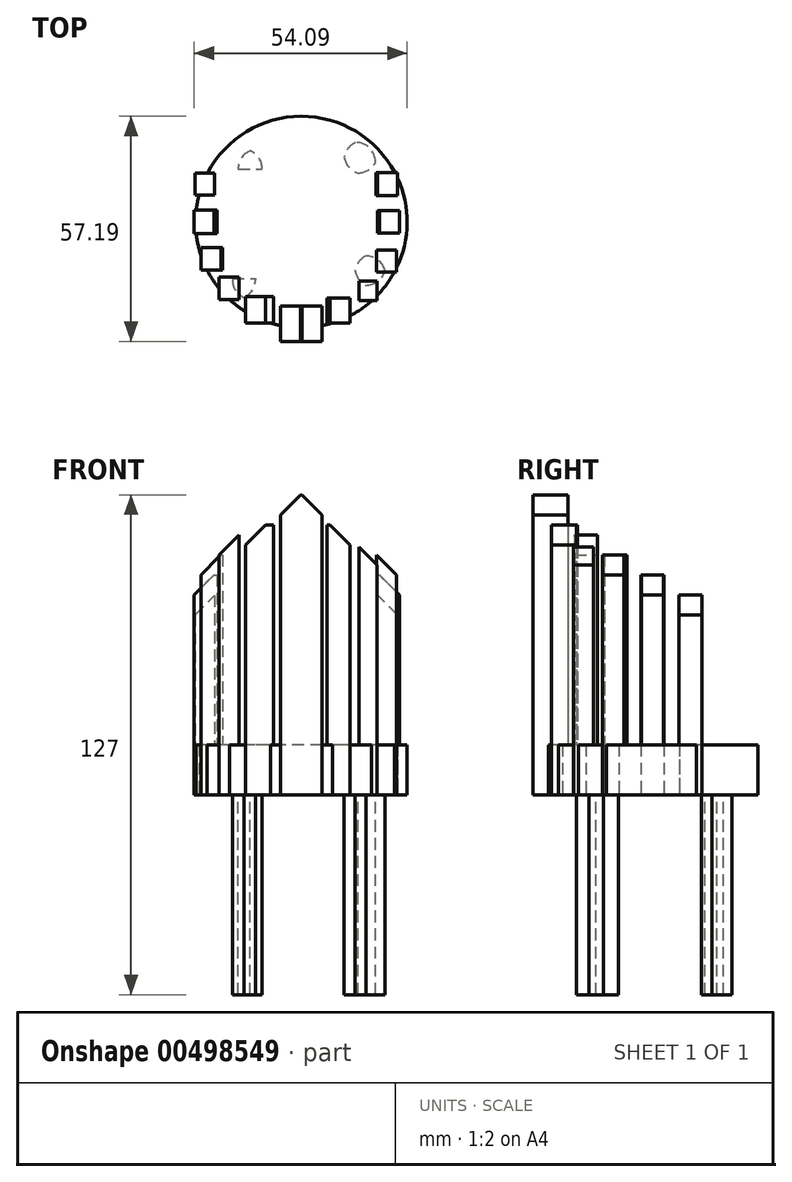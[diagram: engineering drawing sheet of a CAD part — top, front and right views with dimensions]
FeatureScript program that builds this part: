
annotation { "Feature Type Name" : "Feature", "Feature Type Description" : "" }
export const myFeature = defineFeature(function(context is Context, id is Id, definition is map)
    precondition{}
    {
        {
            var Q0;
            Q0=qCreatedBy(makeId("Top.planeOp"),FACE);
            var sketch = newSketch(context, id + "F0", { "sketchPlane" : qUnion([Q0])});
            skCircle(sketch, "E0", {"center": v(0, 0) * mm, "radius": 26.86 * mm});
            skSolve(sketch);
        }
        {
            var Q0;
            Q0=qSketchRegion(id+"F0",true);
            extrude(context, id + "F1", {"entities" : qUnion([Q0]), "depth" : 12.7 * mm});
        }
        {
            var Q0;
            Q0=qCreatedBy(makeId("Top.planeOp"),FACE);
            var sketch = newSketch(context, id + "F2", { "sketchPlane" : qUnion([Q0])});
            skLineSegment(sketch, "E1.bottom", {"start": v(21.46, -16.12) * mm, "end": v(13.6, -16.12) * mm});
            skLineSegment(sketch, "E1.top", {"start": v(21.46, -8.64) * mm, "end": v(13.6, -8.64) * mm});
            skLineSegment(sketch, "E1.left", {"start": v(21.46, -16.12) * mm, "end": v(21.46, -8.64) * mm});
            skLineSegment(sketch, "E1.right", {"start": v(13.6, -16.12) * mm, "end": v(13.6, -8.64) * mm});
            skPoint(sketch, "E1.middle", {"position": v(17.53, -12.38) * mm});
            skSolve(sketch);
        }
        {
            var Q0;
            Q0=qSketchRegion(id+"F2",true);
            extrude(context, id + "F3", {"entities" : qUnion([Q0]), "operationType" : NewBodyOperationType.ADD, "oppositeDirection" : true, "depth" : 50.8 * mm});
        }
        {
            var Q0;
            Q0=qCreatedBy(makeId("Top.planeOp"),FACE);
            var sketch = newSketch(context, id + "F4", { "sketchPlane" : qUnion([Q0])});
            skLineSegment(sketch, "E2.bottom", {"start": v(18.89, 12.44) * mm, "end": v(10.83, 12.44) * mm});
            skLineSegment(sketch, "E2.top", {"start": v(18.89, 20.22) * mm, "end": v(10.83, 20.22) * mm});
            skLineSegment(sketch, "E2.left", {"start": v(18.89, 12.44) * mm, "end": v(18.89, 20.22) * mm});
            skLineSegment(sketch, "E2.right", {"start": v(10.83, 12.44) * mm, "end": v(10.83, 20.22) * mm});
            skPoint(sketch, "E2.middle", {"position": v(14.86, 16.33) * mm});
            skSolve(sketch);
        }
        {
            var Q0;
            Q0=qSketchRegion(id+"F4",true);
            extrude(context, id + "F5", {"entities" : qUnion([Q0]), "operationType" : NewBodyOperationType.ADD, "oppositeDirection" : true, "depth" : 50.8 * mm});
        }
        {
            var Q0;
            Q0=makeQuery(id+"F5.opExtrude","SWEPT_EDGE",EDGE,{"disambiguationData":[OSD([sQuery(id+"F4.wireOp",EDGE,"E2.top"),sQuery(id+"F4.wireOp",EDGE,"E2.left")])]});
            fillet(context, id + "F6", {"entities" : qUnion([Q0]), "radius" : 5.08 * mm, "tangentPropagation" : true, "allowEdgeOverflow" : false});
        }
        {
            var Q0;
            Q0=makeQuery(id+"F5.opExtrude","SWEPT_EDGE",EDGE,{"disambiguationData":[OSD([sQuery(id+"F4.wireOp",EDGE,"E2.bottom"),sQuery(id+"F4.wireOp",EDGE,"E2.left")])]});
            fillet(context, id + "F7", {"entities" : qUnion([Q0]), "radius" : 5.08 * mm, "tangentPropagation" : true, "allowEdgeOverflow" : false});
        }
        {
            var Q0;
            Q0=makeQuery(id+"F3.opExtrude","SWEPT_EDGE",EDGE,{"disambiguationData":[OSD([sQuery(id+"F2.wireOp",EDGE,"E1.bottom"),sQuery(id+"F2.wireOp",EDGE,"E1.left")])]});
            var Q1;
            Q1=makeQuery(id+"F3.opExtrude","SWEPT_EDGE",EDGE,{"disambiguationData":[OSD([sQuery(id+"F2.wireOp",EDGE,"E1.top"),sQuery(id+"F2.wireOp",EDGE,"E1.left")])]});
            fillet(context, id + "F8", {"entities" : qUnion([Q0, Q1]), "radius" : 5.08 * mm, "tangentPropagation" : true, "allowEdgeOverflow" : false});
        }
        {
            var Q0;
            Q0=makeQuery(id+"F5.opExtrude","SWEPT_EDGE",EDGE,{"disambiguationData":[OSD([sQuery(id+"F4.wireOp",EDGE,"E2.top"),sQuery(id+"F4.wireOp",EDGE,"E2.right")])]});
            var Q1;
            Q1=makeQuery(id+"F5.opExtrude","SWEPT_EDGE",EDGE,{"disambiguationData":[OSD([sQuery(id+"F4.wireOp",EDGE,"E2.bottom"),sQuery(id+"F4.wireOp",EDGE,"E2.right")])]});
            var Q2;
            {var subQ0=sQuery(id+"F2.wireOp",EDGE,"E1.top");Q2=makeQuery(id+"F8.opFillet","BLEND_EDGE",EDGE,{"blendedFrom":[makeQuery(id+"F3.opExtrude","SWEPT_EDGE",EDGE,{"disambiguationData":[OSD([subQ0,sQuery(id+"F2.wireOp",EDGE,"E1.left")])]}),makeQuery(id+"F3.opExtrude","SWEPT_FACE",FACE,{"disambiguationData":[OSD([subQ0])]})],"blendedInto":[makeQuery(id+"F3.opExtrude","SWEPT_FACE",FACE,{"disambiguationData":[OSD([subQ0])]})]});}
            var Q3;
            Q3=makeQuery(id+"F3.opExtrude","SWEPT_EDGE",EDGE,{"disambiguationData":[OSD([sQuery(id+"F2.wireOp",EDGE,"E1.bottom"),sQuery(id+"F2.wireOp",EDGE,"E1.right")])]});
            fillet(context, id + "F9", {"entities" : qUnion([Q0, Q1, Q2, Q3]), "radius" : 5.08 * mm, "tangentPropagation" : true, "allowEdgeOverflow" : false});
        }
        {
            var Q0;
            Q0=makeQuery(id+"F3.opExtrude","SWEPT_EDGE",EDGE,{"disambiguationData":[OSD([sQuery(id+"F2.wireOp",EDGE,"E1.top"),sQuery(id+"F2.wireOp",EDGE,"E1.right")])]});
            fillet(context, id + "F10", {"entities" : qUnion([Q0]), "radius" : 5.08 * mm, "tangentPropagation" : true, "allowEdgeOverflow" : false});
        }
        {
            var Q0;
            Q0=qCreatedBy(makeId("Top.planeOp"),FACE);
            var sketch = newSketch(context, id + "F11", { "sketchPlane" : qUnion([Q0])});
            skLineSegment(sketch, "E3.bottom", {"start": v(-16.05, 18.5) * mm, "end": v(-9.93, 18.5) * mm});
            skLineSegment(sketch, "E3.top", {"start": v(-16.05, 13.36) * mm, "end": v(-9.93, 13.36) * mm});
            skLineSegment(sketch, "E3.left", {"start": v(-16.05, 18.5) * mm, "end": v(-16.05, 13.36) * mm});
            skLineSegment(sketch, "E3.right", {"start": v(-9.93, 18.5) * mm, "end": v(-9.93, 13.36) * mm});
            skPoint(sketch, "E3.middle", {"position": v(-12.99, 15.94) * mm});
            skSolve(sketch);
        }
        {
            var Q0;
            Q0=qSketchRegion(id+"F11",true);
            extrude(context, id + "F12", {"entities" : qUnion([Q0]), "operationType" : NewBodyOperationType.ADD, "oppositeDirection" : true, "depth" : 50.8 * mm});
        }
        {
            var Q0;
            Q0=qCreatedBy(makeId("Top.planeOp"),FACE);
            var sketch = newSketch(context, id + "F13", { "sketchPlane" : qUnion([Q0])});
            skLineSegment(sketch, "E4.bottom", {"start": v(-17.51, -14.37) * mm, "end": v(-11.66, -14.37) * mm});
            skLineSegment(sketch, "E4.top", {"start": v(-17.51, -19.72) * mm, "end": v(-11.66, -19.72) * mm});
            skLineSegment(sketch, "E4.left", {"start": v(-17.51, -14.37) * mm, "end": v(-17.51, -19.72) * mm});
            skLineSegment(sketch, "E4.right", {"start": v(-11.66, -14.37) * mm, "end": v(-11.66, -19.72) * mm});
            skPoint(sketch, "E4.middle", {"position": v(-14.59, -17.05) * mm});
            skSolve(sketch);
        }
        {
            var Q0;
            Q0=qSketchRegion(id+"F13",true);
            extrude(context, id + "F14", {"entities" : qUnion([Q0]), "operationType" : NewBodyOperationType.ADD, "oppositeDirection" : true, "depth" : 50.8 * mm});
        }
        {
            var Q0;
            Q0=makeQuery(id+"F14.opExtrude","SWEPT_EDGE",EDGE,{"disambiguationData":[OSD([sQuery(id+"F13.wireOp",EDGE,"E4.top"),sQuery(id+"F13.wireOp",EDGE,"E4.right")])]});
            var Q1;
            Q1=makeQuery(id+"F14.opExtrude","SWEPT_EDGE",EDGE,{"disambiguationData":[OSD([sQuery(id+"F13.wireOp",EDGE,"E4.top"),sQuery(id+"F13.wireOp",EDGE,"E4.left")])]});
            fillet(context, id + "F15", {"entities" : qUnion([Q0, Q1]), "radius" : 5.08 * mm, "tangentPropagation" : true, "allowEdgeOverflow" : false});
        }
        {
            var Q0;
            Q0=makeQuery(id+"F12.opExtrude","SWEPT_EDGE",EDGE,{"disambiguationData":[OSD([sQuery(id+"F11.wireOp",EDGE,"E3.bottom"),sQuery(id+"F11.wireOp",EDGE,"E3.right")])]});
            var Q1;
            Q1=makeQuery(id+"F12.opExtrude","SWEPT_EDGE",EDGE,{"disambiguationData":[OSD([sQuery(id+"F11.wireOp",EDGE,"E3.bottom"),sQuery(id+"F11.wireOp",EDGE,"E3.left")])]});
            fillet(context, id + "F16", {"entities" : qUnion([Q0, Q1]), "radius" : 5.08 * mm, "tangentPropagation" : true, "allowEdgeOverflow" : false});
        }
        {
            var Q0;
            Q0=qCreatedBy(makeId("Top.planeOp"),FACE);
            var sketch = newSketch(context, id + "F17", { "sketchPlane" : qUnion([Q0])});
            skLineSegment(sketch, "E5.bottom", {"start": v(-5.28, -30.33) * mm, "end": v(5.28, -30.33) * mm});
            skLineSegment(sketch, "E5.top", {"start": v(-5.28, -21.41) * mm, "end": v(5.28, -21.41) * mm});
            skLineSegment(sketch, "E5.left", {"start": v(-5.28, -30.33) * mm, "end": v(-5.28, -21.41) * mm});
            skLineSegment(sketch, "E5.right", {"start": v(5.28, -30.33) * mm, "end": v(5.28, -21.41) * mm});
            skPoint(sketch, "E5.middle", {"position": v(0, -25.87) * mm});
            skSolve(sketch);
        }
        {
            var Q0;
            Q0=qSketchRegion(id+"F17",true);
            extrude(context, id + "F18", {"entities" : qUnion([Q0]), "operationType" : NewBodyOperationType.ADD, "depth" : 76.2 * mm});
        }
        {
            var Q0;
            Q0=makeQuery(id+"F18.opExtrude","CAP_EDGE",EDGE,{"disambiguationData":[OSD([sQuery(id+"F17.wireOp",EDGE,"E5.left")])],"isStart":false});
            var Q1;
            Q1=makeQuery(id+"F18.opExtrude","CAP_EDGE",EDGE,{"disambiguationData":[OSD([sQuery(id+"F17.wireOp",EDGE,"E5.right")])],"isStart":false});
            chamfer(context, id + "F19", {"entities" : qUnion([Q0, Q1]), "width" : 5.08 * mm, "tangentPropagation" : true});
        }
        {
            var Q0;
            Q0=qCreatedBy(makeId("Top.planeOp"),FACE);
            var sketch = newSketch(context, id + "F20", { "sketchPlane" : qUnion([Q0])});
            skLineSegment(sketch, "E6.bottom", {"start": v(-14.13, -25.69) * mm, "end": v(-7.1, -25.69) * mm});
            skLineSegment(sketch, "E6.top", {"start": v(-14.13, -18.97) * mm, "end": v(-7.1, -18.97) * mm});
            skLineSegment(sketch, "E6.left", {"start": v(-14.13, -25.69) * mm, "end": v(-14.13, -18.97) * mm});
            skLineSegment(sketch, "E6.right", {"start": v(-7.1, -25.69) * mm, "end": v(-7.1, -18.97) * mm});
            skPoint(sketch, "E6.middle", {"position": v(-10.61, -22.33) * mm});
            skSolve(sketch);
        }
        {
            var Q0;
            Q0=qSketchRegion(id+"F20",true);
            extrude(context, id + "F21", {"entities" : qUnion([Q0]), "operationType" : NewBodyOperationType.ADD, "depth" : 68.58 * mm});
        }
        {
            var Q0;
            Q0=qCreatedBy(makeId("Top.planeOp"),FACE);
            var sketch = newSketch(context, id + "F22", { "sketchPlane" : qUnion([Q0])});
            skLineSegment(sketch, "E7.bottom", {"start": v(6.53, -25.66) * mm, "end": v(12.35, -25.66) * mm});
            skLineSegment(sketch, "E7.top", {"start": v(6.53, -19.34) * mm, "end": v(12.35, -19.34) * mm});
            skLineSegment(sketch, "E7.left", {"start": v(6.53, -25.66) * mm, "end": v(6.53, -19.34) * mm});
            skLineSegment(sketch, "E7.right", {"start": v(12.35, -25.66) * mm, "end": v(12.35, -19.34) * mm});
            skPoint(sketch, "E7.middle", {"position": v(9.44, -22.5) * mm});
            skSolve(sketch);
        }
        {
            var Q0;
            Q0=qSketchRegion(id+"F22",true);
            extrude(context, id + "F23", {"entities" : qUnion([Q0]), "operationType" : NewBodyOperationType.ADD, "depth" : 68.58 * mm});
        }
        {
            var Q0;
            Q0=makeQuery(id+"F23.opExtrude","CAP_EDGE",EDGE,{"disambiguationData":[OSD([sQuery(id+"F22.wireOp",EDGE,"E7.right")])],"isStart":false});
            var Q1;
            Q1=makeQuery(id+"F21.opExtrude","CAP_EDGE",EDGE,{"disambiguationData":[OSD([sQuery(id+"F20.wireOp",EDGE,"E6.left")])],"isStart":false});
            chamfer(context, id + "F24", {"entities" : qUnion([Q0, Q1]), "width" : 5.08 * mm, "tangentPropagation" : true});
        }
        {
            var Q0;
            Q0=qCreatedBy(makeId("Top.planeOp"),FACE);
            var sketch = newSketch(context, id + "F25", { "sketchPlane" : qUnion([Q0])});
            skLineSegment(sketch, "E8.bottom", {"start": v(-20.87, -19.75) * mm, "end": v(-15.87, -19.75) * mm});
            skLineSegment(sketch, "E8.top", {"start": v(-20.87, -14) * mm, "end": v(-15.87, -14) * mm});
            skLineSegment(sketch, "E8.left", {"start": v(-20.87, -19.75) * mm, "end": v(-20.87, -14) * mm});
            skLineSegment(sketch, "E8.right", {"start": v(-15.87, -19.75) * mm, "end": v(-15.87, -14) * mm});
            skPoint(sketch, "E8.middle", {"position": v(-18.37, -16.87) * mm});
            skSolve(sketch);
        }
        {
            var Q0;
            Q0=qSketchRegion(id+"F25",true);
            extrude(context, id + "F26", {"entities" : qUnion([Q0]), "operationType" : NewBodyOperationType.ADD, "depth" : 66.04 * mm});
        }
        {
            var Q0;
            Q0=makeQuery(id+"F26.opExtrude","CAP_EDGE",EDGE,{"disambiguationData":[OSD([sQuery(id+"F25.wireOp",EDGE,"E8.left")])],"isStart":false});
            chamfer(context, id + "F27", {"entities" : qUnion([Q0]), "width" : 5.08 * mm, "tangentPropagation" : true});
        }
        {
            var Q0;
            Q0=qCreatedBy(makeId("Top.planeOp"),FACE);
            var sketch = newSketch(context, id + "F28", { "sketchPlane" : qUnion([Q0])});
            skLineSegment(sketch, "E9.bottom", {"start": v(-25.47, -12.23) * mm, "end": v(-20, -12.23) * mm});
            skLineSegment(sketch, "E9.top", {"start": v(-25.47, -6.5) * mm, "end": v(-20, -6.5) * mm});
            skLineSegment(sketch, "E9.left", {"start": v(-25.47, -12.23) * mm, "end": v(-25.47, -6.5) * mm});
            skLineSegment(sketch, "E9.right", {"start": v(-20, -12.23) * mm, "end": v(-20, -6.5) * mm});
            skPoint(sketch, "E9.middle", {"position": v(-22.74, -9.37) * mm});
            skSolve(sketch);
        }
        {
            var Q0;
            Q0=qSketchRegion(id+"F28",true);
            extrude(context, id + "F29", {"entities" : qUnion([Q0]), "operationType" : NewBodyOperationType.ADD, "depth" : 60.96 * mm});
        }
        {
            var Q0;
            Q0=makeQuery(id+"F29.opExtrude","CAP_EDGE",EDGE,{"disambiguationData":[OSD([sQuery(id+"F28.wireOp",EDGE,"E9.left")])],"isStart":false});
            chamfer(context, id + "F30", {"entities" : qUnion([Q0]), "width" : 5.08 * mm, "tangentPropagation" : true});
        }
        {
            var Q0;
            Q0=qCreatedBy(makeId("Top.planeOp"),FACE);
            var sketch = newSketch(context, id + "F31", { "sketchPlane" : qUnion([Q0])});
            skLineSegment(sketch, "E10.bottom", {"start": v(-27.23, -2.95) * mm, "end": v(-21.46, -2.95) * mm});
            skLineSegment(sketch, "E10.top", {"start": v(-27.23, 2.95) * mm, "end": v(-21.46, 2.95) * mm});
            skLineSegment(sketch, "E10.left", {"start": v(-27.23, -2.95) * mm, "end": v(-27.23, 2.95) * mm});
            skLineSegment(sketch, "E10.right", {"start": v(-21.46, -2.95) * mm, "end": v(-21.46, 2.95) * mm});
            skPoint(sketch, "E10.middle", {"position": v(-24.35, 0) * mm});
            skSolve(sketch);
        }
        {
            var Q0;
            Q0=qCreatedBy(makeId("Top.planeOp"),FACE);
            var sketch = newSketch(context, id + "F32", { "sketchPlane" : qUnion([Q0])});
            skLineSegment(sketch, "E11.bottom", {"start": v(-26.94, 6.87) * mm, "end": v(-22, 6.87) * mm});
            skLineSegment(sketch, "E11.top", {"start": v(-26.94, 12.45) * mm, "end": v(-22, 12.45) * mm});
            skLineSegment(sketch, "E11.left", {"start": v(-26.94, 6.87) * mm, "end": v(-26.94, 12.45) * mm});
            skLineSegment(sketch, "E11.right", {"start": v(-22, 6.87) * mm, "end": v(-22, 12.45) * mm});
            skPoint(sketch, "E11.middle", {"position": v(-24.47, 9.66) * mm});
            skSolve(sketch);
        }
        {
            var Q0;
            Q0=qSketchRegion(id+"F31",true);
            extrude(context, id + "F33", {"entities" : qUnion([Q0]), "operationType" : NewBodyOperationType.ADD, "depth" : 55.88 * mm});
        }
        {
            var Q0;
            Q0=qSketchRegion(id+"F32",true);
            extrude(context, id + "F34", {"entities" : qUnion([Q0]), "operationType" : NewBodyOperationType.ADD, "depth" : 50.8 * mm});
        }
        {
            var Q0;
            Q0=makeQuery(id+"F33.opExtrude","CAP_EDGE",EDGE,{"disambiguationData":[OSD([sQuery(id+"F31.wireOp",EDGE,"E10.left")])],"isStart":false});
            chamfer(context, id + "F35", {"entities" : qUnion([Q0]), "width" : 5.08 * mm, "tangentPropagation" : true});
        }
        {
            var Q0;
            Q0=makeQuery(id+"F34.opExtrude","CAP_EDGE",EDGE,{"disambiguationData":[OSD([sQuery(id+"F32.wireOp",EDGE,"E11.left")])],"isStart":false});
            chamfer(context, id + "F36", {"entities" : qUnion([Q0]), "width" : 5.08 * mm, "tangentPropagation" : true});
        }
        {
            var Q0;
            Q0=qCreatedBy(makeId("Top.planeOp"),FACE);
            var sketch = newSketch(context, id + "F37", { "sketchPlane" : qUnion([Q0])});
            skLineSegment(sketch, "E12.bottom", {"start": v(14.7, -20.04) * mm, "end": v(19.27, -20.04) * mm});
            skLineSegment(sketch, "E12.top", {"start": v(14.7, -14.97) * mm, "end": v(19.27, -14.97) * mm});
            skLineSegment(sketch, "E12.left", {"start": v(14.7, -20.04) * mm, "end": v(14.7, -14.97) * mm});
            skLineSegment(sketch, "E12.right", {"start": v(19.27, -20.04) * mm, "end": v(19.27, -14.97) * mm});
            skPoint(sketch, "E12.middle", {"position": v(16.99, -17.5) * mm});
            skSolve(sketch);
        }
        {
            var Q0;
            Q0=qCreatedBy(makeId("Top.planeOp"),FACE);
            var sketch = newSketch(context, id + "F38", { "sketchPlane" : qUnion([Q0])});
            skLineSegment(sketch, "E13.bottom", {"start": v(19.16, -12.73) * mm, "end": v(24.2, -12.73) * mm});
            skLineSegment(sketch, "E13.top", {"start": v(19.16, -7.16) * mm, "end": v(24.2, -7.16) * mm});
            skLineSegment(sketch, "E13.left", {"start": v(19.16, -12.73) * mm, "end": v(19.16, -7.16) * mm});
            skLineSegment(sketch, "E13.right", {"start": v(24.2, -12.73) * mm, "end": v(24.2, -7.16) * mm});
            skPoint(sketch, "E13.middle", {"position": v(21.68, -9.94) * mm});
            skSolve(sketch);
        }
        {
            var Q0;
            Q0=qCreatedBy(makeId("Top.planeOp"),FACE);
            var sketch = newSketch(context, id + "F39", { "sketchPlane" : qUnion([Q0])});
            skLineSegment(sketch, "E14.bottom", {"start": v(19.3, -2.83) * mm, "end": v(24.9, -2.83) * mm});
            skLineSegment(sketch, "E14.top", {"start": v(19.3, 2.83) * mm, "end": v(24.9, 2.83) * mm});
            skLineSegment(sketch, "E14.left", {"start": v(19.3, -2.83) * mm, "end": v(19.3, 2.83) * mm});
            skLineSegment(sketch, "E14.right", {"start": v(24.9, -2.83) * mm, "end": v(24.9, 2.83) * mm});
            skPoint(sketch, "E14.middle", {"position": v(22.1, 0) * mm});
            skSolve(sketch);
        }
        {
            var Q0;
            Q0=qCreatedBy(makeId("Top.planeOp"),FACE);
            var sketch = newSketch(context, id + "F40", { "sketchPlane" : qUnion([Q0])});
            skLineSegment(sketch, "E15.bottom", {"start": v(18.93, 6.74) * mm, "end": v(24.44, 6.74) * mm});
            skLineSegment(sketch, "E15.top", {"start": v(18.93, 12.55) * mm, "end": v(24.44, 12.55) * mm});
            skLineSegment(sketch, "E15.left", {"start": v(18.93, 6.74) * mm, "end": v(18.93, 12.55) * mm});
            skLineSegment(sketch, "E15.right", {"start": v(24.44, 6.74) * mm, "end": v(24.44, 12.55) * mm});
            skPoint(sketch, "E15.middle", {"position": v(21.69, 9.64) * mm});
            skSolve(sketch);
        }
        {
            var Q0;
            Q0=qSketchRegion(id+"F37",true);
            extrude(context, id + "F41", {"entities" : qUnion([Q0]), "operationType" : NewBodyOperationType.ADD, "depth" : 63.5 * mm});
        }
        {
            var Q0;
            Q0=qSketchRegion(id+"F38",true);
            extrude(context, id + "F42", {"entities" : qUnion([Q0]), "operationType" : NewBodyOperationType.ADD, "depth" : 60.96 * mm});
        }
        {
            var Q0;
            Q0=qSketchRegion(id+"F39",true);
            extrude(context, id + "F43", {"entities" : qUnion([Q0]), "operationType" : NewBodyOperationType.ADD, "depth" : 55.88 * mm});
        }
        {
            var Q0;
            Q0=qSketchRegion(id+"F40",true);
            extrude(context, id + "F44", {"entities" : qUnion([Q0]), "operationType" : NewBodyOperationType.ADD, "depth" : 50.8 * mm});
        }
        {
            var Q0;
            Q0=makeQuery(id+"F41.opExtrude","CAP_EDGE",EDGE,{"disambiguationData":[OSD([sQuery(id+"F37.wireOp",EDGE,"E12.right")])],"isStart":false});
            var Q1;
            Q1=makeQuery(id+"F42.opExtrude","CAP_EDGE",EDGE,{"disambiguationData":[OSD([sQuery(id+"F38.wireOp",EDGE,"E13.right")])],"isStart":false});
            var Q2;
            Q2=makeQuery(id+"F43.opExtrude","CAP_EDGE",EDGE,{"disambiguationData":[OSD([sQuery(id+"F39.wireOp",EDGE,"E14.right")])],"isStart":false});
            var Q3;
            Q3=makeQuery(id+"F44.opExtrude","CAP_EDGE",EDGE,{"disambiguationData":[OSD([sQuery(id+"F40.wireOp",EDGE,"E15.right")])],"isStart":false});
            chamfer(context, id + "F45", {"entities" : qUnion([Q0, Q1, Q2, Q3]), "width" : 5.08 * mm, "tangentPropagation" : true});
        }
    });
